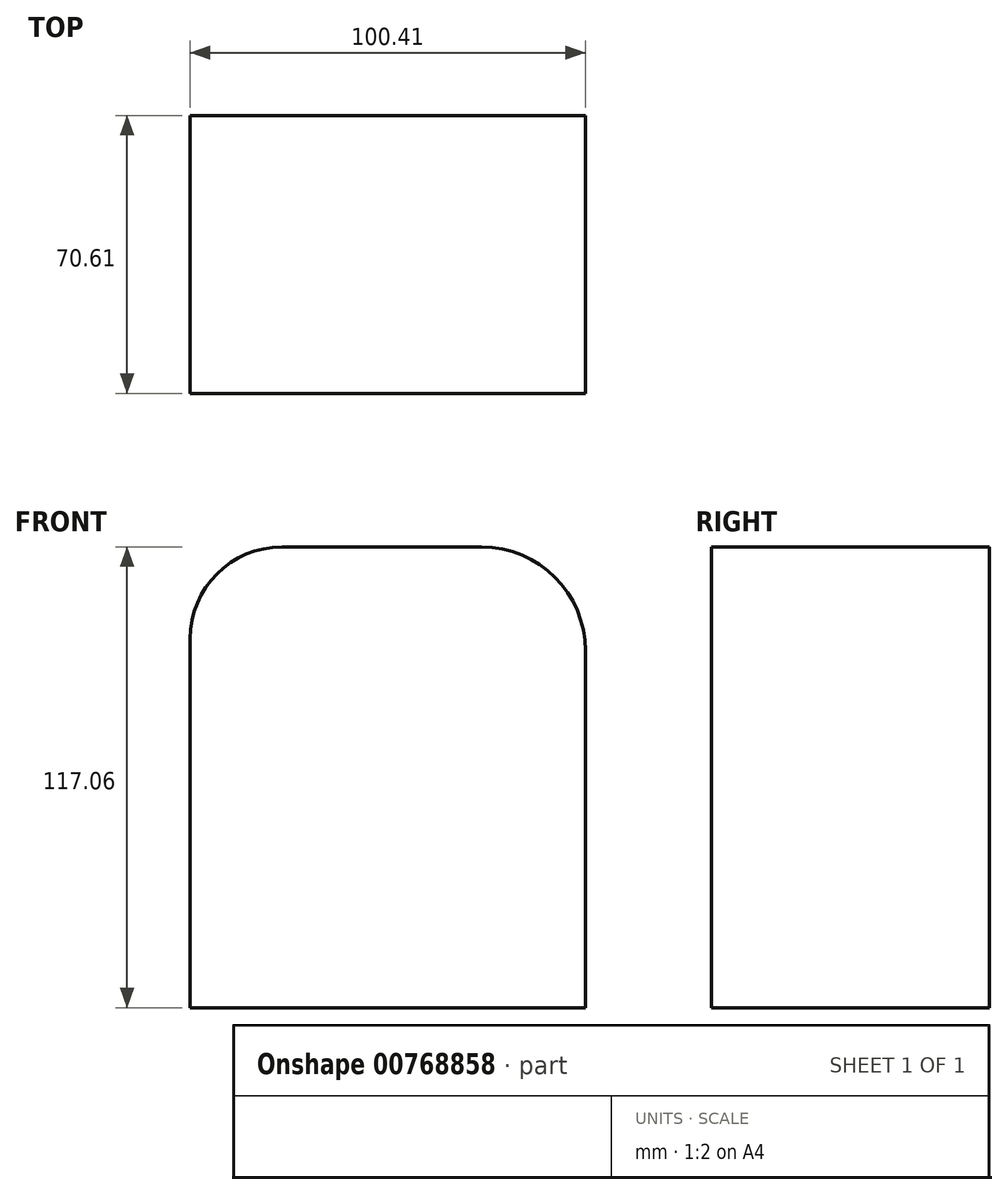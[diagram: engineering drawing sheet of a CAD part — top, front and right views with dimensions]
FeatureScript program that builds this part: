
annotation { "Feature Type Name" : "Feature", "Feature Type Description" : "" }
export const myFeature = defineFeature(function(context is Context, id is Id, definition is map)
    precondition{}
    {
        {
            var Q0;
            Q0=qCreatedBy(makeId("Front.planeOp"),FACE);
            var sketch = newSketch(context, id + "F0", { "sketchPlane" : qUnion([Q0])});
            skLineSegment(sketch, "E0.bottom", {"start": v(-44.97, 41.21) * mm, "end": v(55.44, 41.21) * mm});
            skLineSegment(sketch, "E0.top", {"start": v(-44.97, -75.85) * mm, "end": v(55.44, -75.85) * mm});
            skLineSegment(sketch, "E0.left", {"start": v(-44.97, 41.21) * mm, "end": v(-44.97, -75.85) * mm});
            skLineSegment(sketch, "E0.right", {"start": v(55.44, 41.21) * mm, "end": v(55.44, -75.85) * mm});
            skSolve(sketch);
        }
        {
            var Q0;
            Q0=makeQuery(id+"F0.imprint","IMPRINT",FACE,{"disambiguationData":[TD([[makeQuery(id+"F0.imprint","IMPRINT",EDGE,{"derivedFrom":sQuery(id+"F0.wireOp",EDGE,"E0.bottom")}),-1.0]])]});
            extrude(context, id + "F1", {"entities" : qUnion([Q0]), "depth" : 70.61 * mm, "offsetDistance" : 25.4 * mm});
        }
        {
            var Q0;
            Q0=makeQuery(id+"F1.opExtrude","SWEPT_EDGE",EDGE,{"disambiguationData":[OSD([sQuery(id+"F0.wireOp",EDGE,"E0.bottom"),sQuery(id+"F0.wireOp",EDGE,"E0.left")])]});
            fillet(context, id + "F2", {"entities" : qUnion([Q0]), "radius" : 23.3 * mm, "tangentPropagation" : true, "allowEdgeOverflow" : false});
        }
        {
            var Q0;
            Q0=makeQuery(id+"F1.opExtrude","SWEPT_EDGE",EDGE,{"disambiguationData":[OSD([sQuery(id+"F0.wireOp",EDGE,"E0.bottom"),sQuery(id+"F0.wireOp",EDGE,"E0.right")])]});
            fillet(context, id + "F3", {"entities" : qUnion([Q0]), "radius" : 26.37 * mm, "tangentPropagation" : true, "allowEdgeOverflow" : false});
        }
    });
